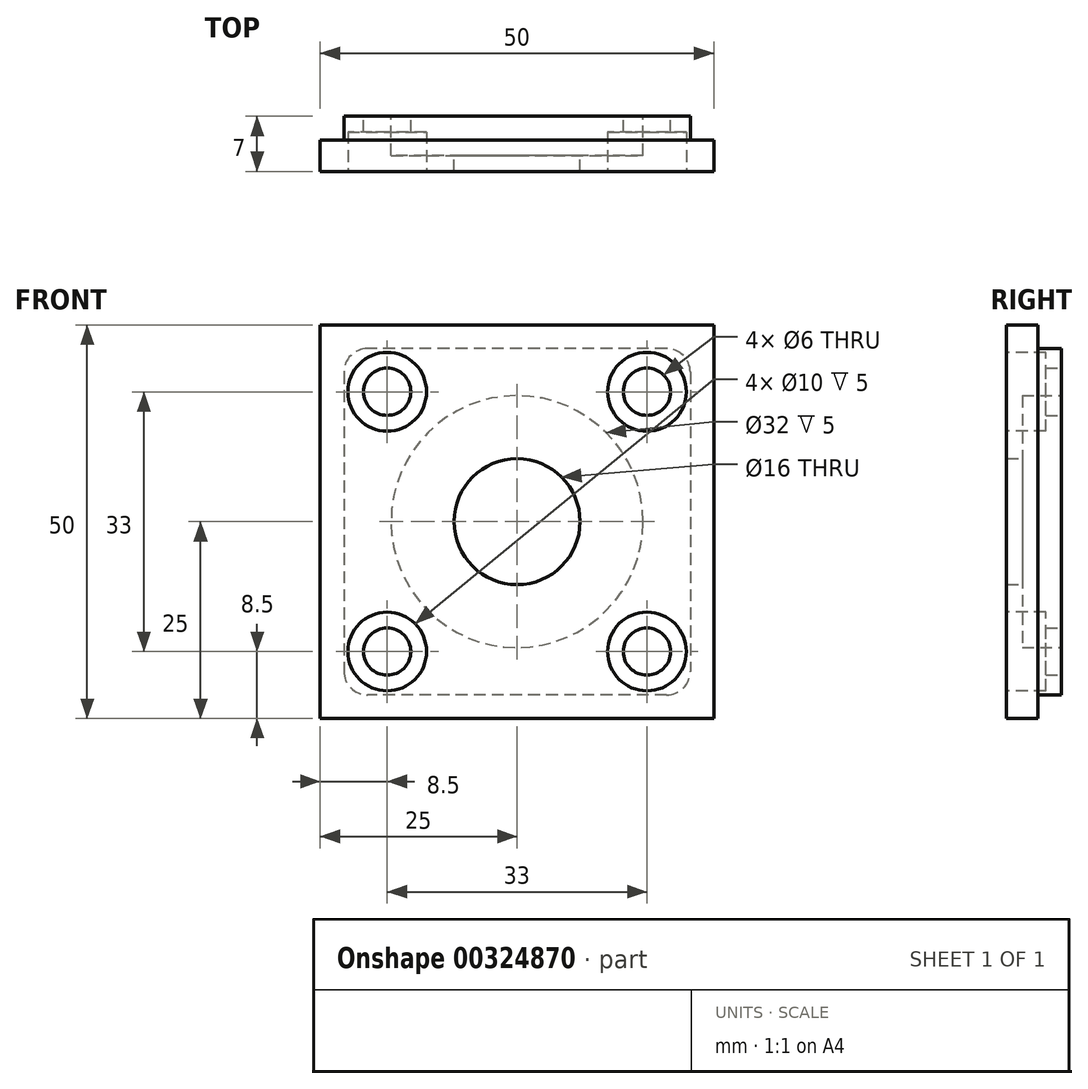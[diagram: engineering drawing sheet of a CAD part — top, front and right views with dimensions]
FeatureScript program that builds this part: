
annotation { "Feature Type Name" : "Feature", "Feature Type Description" : "" }
export const myFeature = defineFeature(function(context is Context, id is Id, definition is map)
    precondition{}
    {
        {
            var Q0;
            Q0=qCreatedBy(makeId("Front.planeOp"),FACE);
            var sketch = newSketch(context, id + "F0", { "sketchPlane" : qUnion([Q0])});
            skLineSegment(sketch, "E0.bottom", {"start": v(-25, 25) * mm, "end": v(25, 25) * mm});
            skLineSegment(sketch, "E0.top", {"start": v(-25, -25) * mm, "end": v(25, -25) * mm});
            skLineSegment(sketch, "E0.left", {"start": v(-25, 25) * mm, "end": v(-25, -25) * mm});
            skLineSegment(sketch, "E0.right", {"start": v(25, 25) * mm, "end": v(25, -25) * mm});
            skPoint(sketch, "E0.middle", {"position": v(0, 0) * mm});
            skSolve(sketch);
        }
        {
            var Q0;
            Q0=makeQuery(id+"F0.imprint","IMPRINT",FACE,{"disambiguationData":[TD([[makeQuery(id+"F0.imprint","IMPRINT",EDGE,{"derivedFrom":sQuery(id+"F0.wireOp",EDGE,"E0.bottom")}),-1.0]])]});
            extrude(context, id + "F1", {"entities" : qUnion([Q0]), "oppositeDirection" : true, "depth" : 4 * mm});
        }
        {
            var Q0;
            Q0=makeQuery(id+"F1.opExtrude","CAP_FACE",FACE,{"disambiguationData":[OSD([sQuery(id+"F0.wireOp",EDGE,"E0.bottom"),sQuery(id+"F0.wireOp",EDGE,"E0.top"),sQuery(id+"F0.wireOp",EDGE,"E0.left"),sQuery(id+"F0.wireOp",EDGE,"E0.right")])],"isStart":false});
            var sketch = newSketch(context, id + "F2", { "sketchPlane" : qUnion([Q0])});
            skLineSegment(sketch, "E1.bottom", {"start": v(-22, 22) * mm, "end": v(22, 22) * mm});
            skLineSegment(sketch, "E1.top", {"start": v(-22, -22) * mm, "end": v(22, -22) * mm});
            skLineSegment(sketch, "E1.left", {"start": v(-22, 22) * mm, "end": v(-22, -22) * mm});
            skLineSegment(sketch, "E1.right", {"start": v(22, 22) * mm, "end": v(22, -22) * mm});
            skPoint(sketch, "E1.middle", {"position": v(0, 0) * mm});
            skSolve(sketch);
        }
        {
            var Q0;
            Q0=makeQuery(id+"F2.imprint","IMPRINT",FACE,{"disambiguationData":[TD([[makeQuery(id+"F2.imprint","IMPRINT",EDGE,{"derivedFrom":sQuery(id+"F2.wireOp",EDGE,"E1.bottom")}),-1.0]])]});
            extrude(context, id + "F3", {"entities" : qUnion([Q0]), "operationType" : NewBodyOperationType.ADD, "depth" : 3 * mm});
        }
        {
            var Q0;
            Q0=makeQuery(id+"F3.opExtrude","CAP_FACE",FACE,{"disambiguationData":[OSD([sQuery(id+"F2.wireOp",EDGE,"E1.bottom"),sQuery(id+"F2.wireOp",EDGE,"E1.top"),sQuery(id+"F2.wireOp",EDGE,"E1.left"),sQuery(id+"F2.wireOp",EDGE,"E1.right")])],"isStart":false});
            var sketch = newSketch(context, id + "F4", { "sketchPlane" : qUnion([Q0])});
            skLineSegment(sketch, "E2", {"start": v(-22, 22) * mm, "end": v(22, -22) * mm, "construction": true});
            skLineSegment(sketch, "E3", {"start": v(22, 22) * mm, "end": v(-22, -22) * mm, "construction": true});
            skLineSegment(sketch, "E4.bottom", {"start": v(-16.5, 16.5) * mm, "end": v(16.5, 16.5) * mm, "construction": true});
            skLineSegment(sketch, "E4.top", {"start": v(-16.5, -16.5) * mm, "end": v(16.5, -16.5) * mm, "construction": true});
            skLineSegment(sketch, "E4.left", {"start": v(-16.5, 16.5) * mm, "end": v(-16.5, -16.5) * mm, "construction": true});
            skLineSegment(sketch, "E4.right", {"start": v(16.5, 16.5) * mm, "end": v(16.5, -16.5) * mm, "construction": true});
            skPoint(sketch, "E4.middle", {"position": v(0, 0) * mm});
            skCircle(sketch, "E5", {"center": v(-16.5, 16.5) * mm, "radius": 3 * mm});
            skCircle(sketch, "E6", {"center": v(16.5, 16.5) * mm, "radius": 3 * mm});
            skCircle(sketch, "E7", {"center": v(-16.5, -16.5) * mm, "radius": 3 * mm});
            skCircle(sketch, "E8", {"center": v(16.5, -16.5) * mm, "radius": 3 * mm});
            skSolve(sketch);
        }
        {
            var Q0;
            Q0=makeQuery(id+"F4.imprint","IMPRINT",FACE,{"disambiguationData":[TD([[makeQuery(id+"F4.imprint","IMPRINT",EDGE,{"derivedFrom":sQuery(id+"F4.wireOp",EDGE,"E5")}),1.0]])]});
            var Q1;
            Q1=makeQuery(id+"F4.imprint","IMPRINT",FACE,{"disambiguationData":[TD([[makeQuery(id+"F4.imprint","IMPRINT",EDGE,{"derivedFrom":sQuery(id+"F4.wireOp",EDGE,"E6")}),1.0]])]});
            var Q2;
            Q2=makeQuery(id+"F4.imprint","IMPRINT",FACE,{"disambiguationData":[TD([[makeQuery(id+"F4.imprint","IMPRINT",EDGE,{"derivedFrom":sQuery(id+"F4.wireOp",EDGE,"E8")}),1.0]])]});
            var Q3;
            Q3=makeQuery(id+"F4.imprint","IMPRINT",FACE,{"disambiguationData":[TD([[makeQuery(id+"F4.imprint","IMPRINT",EDGE,{"derivedFrom":sQuery(id+"F4.wireOp",EDGE,"E7")}),1.0]])]});
            var Q4;
            Q4=makeQuery(id+"F4.imprint","IMPRINT",FACE,{"disambiguationData":[TD([[makeQuery(id+"F4.imprint","IMPRINT",EDGE,{"derivedFrom":sQuery(id+"F4.wireOp",EDGE,"QwKJkzou-eQ0R-DmLM-VaWs-TZL8aThNHikG")}),1.0]])]});
            extrude(context, id + "F5", {"entities" : qUnion([Q0, Q1, Q2, Q3, Q4]), "operationType" : NewBodyOperationType.REMOVE, "oppositeDirection" : true, "depth" : 25 * mm});
        }
        {
            var Q0;
            Q0=makeQuery(id+"F1.opExtrude","CAP_FACE",FACE,{"disambiguationData":[OSD([sQuery(id+"F0.wireOp",EDGE,"E0.bottom"),sQuery(id+"F0.wireOp",EDGE,"E0.top"),sQuery(id+"F0.wireOp",EDGE,"E0.left"),sQuery(id+"F0.wireOp",EDGE,"E0.right")])],"isStart":true});
            var sketch = newSketch(context, id + "F6", { "sketchPlane" : qUnion([Q0])});
            skCircle(sketch, "E9", {"center": v(-16.5, 16.5) * mm, "radius": 5 * mm});
            skCircle(sketch, "E10.1.0", {"center": v(-16.5, -16.5) * mm, "radius": 5 * mm});
            skCircle(sketch, "E10.2.0", {"center": v(16.5, -16.5) * mm, "radius": 5 * mm});
            skCircle(sketch, "E10.3.0", {"center": v(16.5, 16.5) * mm, "radius": 5 * mm});
            skPoint(sketch, "E10.center", {"position": v(0, 0) * mm});
            skSolve(sketch);
        }
        {
            var Q0;
            Q0=makeQuery(id+"F6.imprint","IMPRINT",FACE,{"disambiguationData":[TD([[makeQuery(id+"F6.imprint","IMPRINT",EDGE,{"derivedFrom":sQuery(id+"F6.wireOp",EDGE,"E9")}),1.0]])]});
            var Q1;
            Q1=makeQuery(id+"F6.imprint","IMPRINT",FACE,{"disambiguationData":[TD([[makeQuery(id+"F6.imprint","IMPRINT",EDGE,{"derivedFrom":sQuery(id+"F6.wireOp",EDGE,"E10.3.0")}),1.0]])]});
            var Q2;
            Q2=makeQuery(id+"F6.imprint","IMPRINT",FACE,{"disambiguationData":[TD([[makeQuery(id+"F6.imprint","IMPRINT",EDGE,{"derivedFrom":sQuery(id+"F6.wireOp",EDGE,"E10.2.0")}),1.0]])]});
            var Q3;
            Q3=makeQuery(id+"F6.imprint","IMPRINT",FACE,{"disambiguationData":[TD([[makeQuery(id+"F6.imprint","IMPRINT",EDGE,{"derivedFrom":sQuery(id+"F6.wireOp",EDGE,"E10.1.0")}),1.0]])]});
            extrude(context, id + "F7", {"entities" : qUnion([Q0, Q1, Q2, Q3]), "operationType" : NewBodyOperationType.REMOVE, "oppositeDirection" : true, "depth" : 5 * mm});
        }
        {
            var Q0;
            Q0=makeQuery(id+"F3.opExtrude","CAP_FACE",FACE,{"disambiguationData":[OSD([sQuery(id+"F2.wireOp",EDGE,"E1.bottom"),sQuery(id+"F2.wireOp",EDGE,"E1.top"),sQuery(id+"F2.wireOp",EDGE,"E1.left"),sQuery(id+"F2.wireOp",EDGE,"E1.right")])],"isStart":false});
            var sketch = newSketch(context, id + "F8", { "sketchPlane" : qUnion([Q0])});
            skCircle(sketch, "E11", {"center": v(0, 0) * mm, "radius": 16 * mm});
            skSolve(sketch);
        }
        {
            var Q0;
            Q0=makeQuery(id+"F8.imprint","IMPRINT",FACE,{"disambiguationData":[TD([[makeQuery(id+"F8.imprint","IMPRINT",EDGE,{"derivedFrom":sQuery(id+"F8.wireOp",EDGE,"E11")}),1.0]])]});
            extrude(context, id + "F9", {"entities" : qUnion([Q0]), "operationType" : NewBodyOperationType.REMOVE, "oppositeDirection" : true, "depth" : 5 * mm});
        }
        {
            var Q0;
            Q0=makeQuery(id+"F9.boolean.opBoolean","COPY",FACE,{"derivedFrom":makeQuery(id+"F9.opExtrude","CAP_FACE",FACE,{"disambiguationData":[OSD([sQuery(id+"F8.wireOp",EDGE,"E11")])],"isStart":false})});
            var sketch = newSketch(context, id + "F10", { "sketchPlane" : qUnion([Q0])});
            skCircle(sketch, "E12", {"center": v(0, 0) * mm, "radius": 8 * mm});
            skSolve(sketch);
        }
        {
            var Q0;
            Q0=makeQuery(id+"F10.imprint","IMPRINT",FACE,{"disambiguationData":[TD([[makeQuery(id+"F10.imprint","IMPRINT",EDGE,{"derivedFrom":sQuery(id+"F10.wireOp",EDGE,"E12")}),1.0]])]});
            extrude(context, id + "F11", {"entities" : qUnion([Q0]), "operationType" : NewBodyOperationType.REMOVE, "oppositeDirection" : true, "depth" : 25 * mm});
        }
        {
            var Q0;
            Q0=makeQuery(id+"F3.opExtrude","SWEPT_EDGE",EDGE,{"disambiguationData":[OSD([sQuery(id+"F2.wireOp",EDGE,"E1.bottom"),sQuery(id+"F2.wireOp",EDGE,"E1.right")])]});
            var Q1;
            Q1=makeQuery(id+"F3.opExtrude","SWEPT_EDGE",EDGE,{"disambiguationData":[OSD([sQuery(id+"F2.wireOp",EDGE,"E1.top"),sQuery(id+"F2.wireOp",EDGE,"E1.right")])]});
            var Q2;
            Q2=makeQuery(id+"F3.opExtrude","SWEPT_EDGE",EDGE,{"disambiguationData":[OSD([sQuery(id+"F2.wireOp",EDGE,"E1.top"),sQuery(id+"F2.wireOp",EDGE,"E1.left")])]});
            var Q3;
            Q3=makeQuery(id+"F3.opExtrude","SWEPT_EDGE",EDGE,{"disambiguationData":[OSD([sQuery(id+"F2.wireOp",EDGE,"E1.bottom"),sQuery(id+"F2.wireOp",EDGE,"E1.left")])]});
            fillet(context, id + "F12", {"entities" : qUnion([Q0, Q1, Q2, Q3]), "radius" : 3 * mm, "tangentPropagation" : true, "allowEdgeOverflow" : false});
        }
    });
